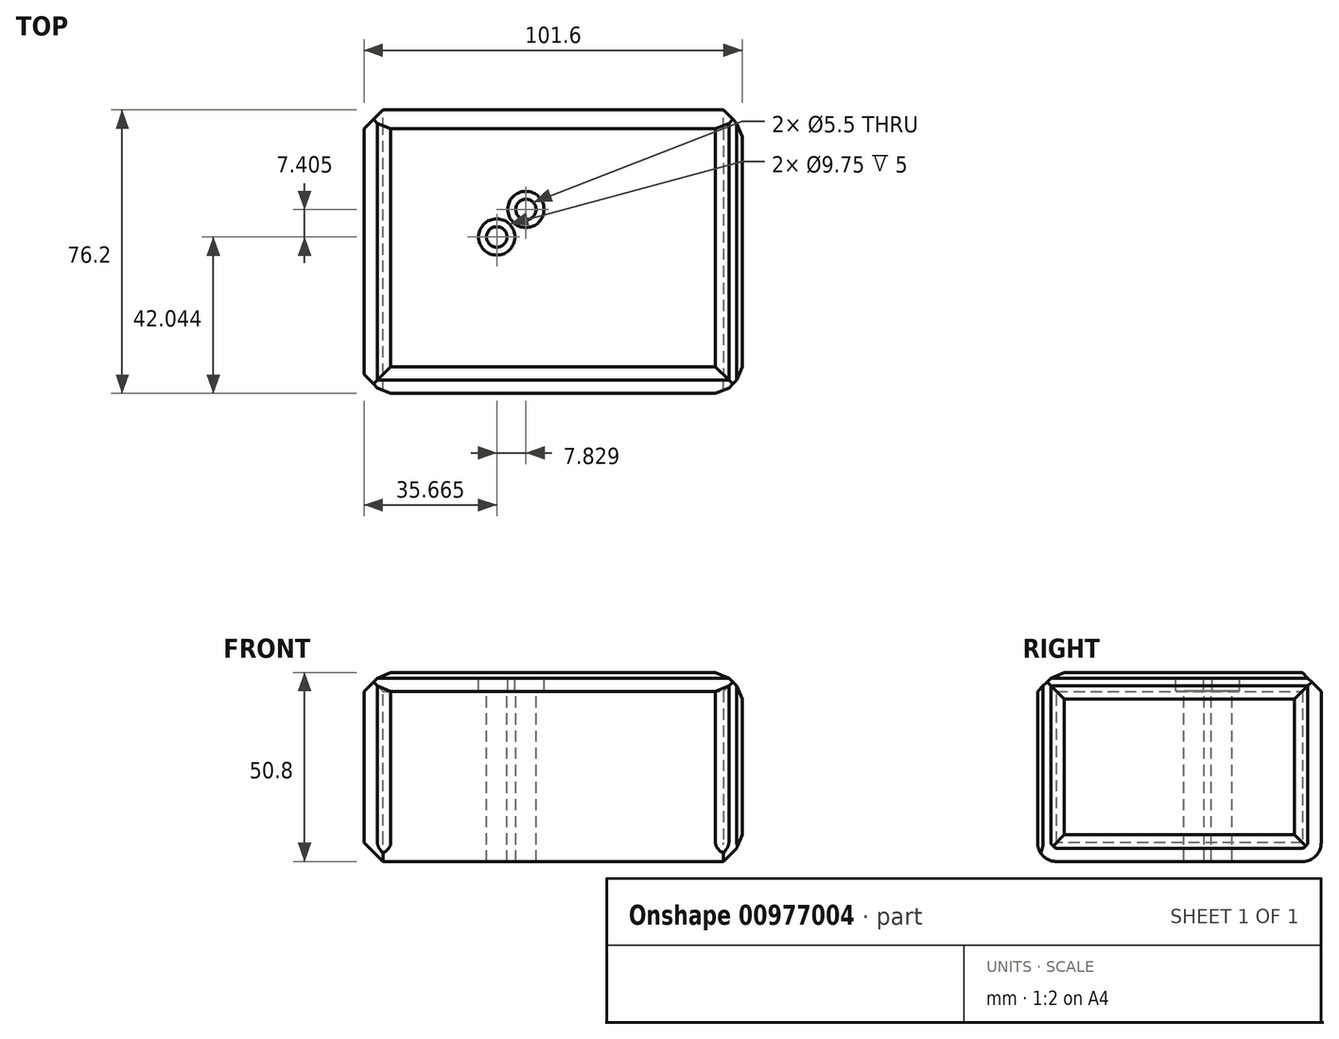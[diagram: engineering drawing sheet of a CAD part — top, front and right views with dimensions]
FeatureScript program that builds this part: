
annotation { "Feature Type Name" : "Feature", "Feature Type Description" : "" }
export const myFeature = defineFeature(function(context is Context, id is Id, definition is map)
    precondition{}
    {
        {
            var Q0;
            Q0=qCreatedBy(makeId("Top.planeOp"),FACE);
            var sketch = newSketch(context, id + "F0", { "sketchPlane" : qUnion([Q0])});
            skLineSegment(sketch, "E0.bottom", {"start": v(50.8, 38.1) * mm, "end": v(-50.8, 38.1) * mm});
            skLineSegment(sketch, "E0.top", {"start": v(50.8, -38.1) * mm, "end": v(-50.8, -38.1) * mm});
            skLineSegment(sketch, "E0.left", {"start": v(50.8, 38.1) * mm, "end": v(50.8, -38.1) * mm});
            skLineSegment(sketch, "E0.right", {"start": v(-50.8, 38.1) * mm, "end": v(-50.8, -38.1) * mm});
            skPoint(sketch, "E0.middle", {"position": v(0, 0) * mm});
            skCircle(sketch, "E1", {"center": v(0, -4.6) * mm, "radius": 3.99 * mm});
            skCircle(sketch, "E2", {"center": v(0, -4.6) * mm, "radius": 22.85 * mm});
            skSolve(sketch);
        }
        {
            var Q0;
            Q0=makeQuery(id+"F0.imprint","IMPRINT",FACE,{"disambiguationData":[TD([[makeQuery(id+"F0.imprint","IMPRINT",EDGE,{"derivedFrom":sQuery(id+"F0.wireOp",EDGE,"E0.bottom")}),1.0]])]});
            var Q1;
            Q1=makeQuery(id+"F0.imprint","IMPRINT",FACE,{"disambiguationData":[TD([[makeQuery(id+"F0.imprint","IMPRINT",EDGE,{"derivedFrom":sQuery(id+"F0.wireOp",EDGE,"E1")}),1.0]])]});
            var Q2;
            Q2=makeQuery(id+"F0.imprint","IMPRINT",FACE,{"disambiguationData":[TD([[makeQuery(id+"F0.imprint","IMPRINT",EDGE,{"derivedFrom":sQuery(id+"F0.wireOp",EDGE,"E1")}),-1.0]])]});
            extrude(context, id + "F1", {"entities" : qUnion([Q0, Q1, Q2]), "depth" : 50.8 * mm, "offsetDistance" : 25.4 * mm});
        }
        {
            var Q0;
            Q0=makeQuery(id+"F1.opExtrude","CAP_EDGE",EDGE,{"disambiguationData":[OSD([sQuery(id+"F0.wireOp",EDGE,"E0.bottom")])],"isStart":true});
            fillet(context, id + "F2", {"entities" : qUnion([Q0]), "radius" : 5.08 * mm, "tangentPropagation" : true, "allowEdgeOverflow" : false});
        }
        {
            var Q0;
            Q0=makeQuery(id+"F1.opExtrude","CAP_EDGE",EDGE,{"disambiguationData":[OSD([sQuery(id+"F0.wireOp",EDGE,"E0.top")])],"isStart":true});
            fillet(context, id + "F3", {"entities" : qUnion([Q0]), "radius" : 5.08 * mm, "tangentPropagation" : true, "allowEdgeOverflow" : false});
        }
        {
            var Q0;
            Q0=makeQuery(id+"F1.opExtrude","SWEPT_FACE",FACE,{"disambiguationData":[OSD([sQuery(id+"F0.wireOp",EDGE,"E0.left")])]});
            chamfer(context, id + "F4", {"entities" : qUnion([Q0]), "width" : 5.08 * mm, "tangentPropagation" : true});
        }
        {
            var Q0;
            Q0=makeQuery(id+"F1.opExtrude","SWEPT_FACE",FACE,{"disambiguationData":[OSD([sQuery(id+"F0.wireOp",EDGE,"E0.right")])]});
            chamfer(context, id + "F5", {"entities" : qUnion([Q0]), "width" : 5.08 * mm, "tangentPropagation" : true});
        }
        {
            var Q0;
            Q0=makeQuery(id+"F1.opExtrude","SWEPT_FACE",FACE,{"disambiguationData":[OSD([sQuery(id+"F0.wireOp",EDGE,"E0.top")])]});
            chamfer(context, id + "F6", {"entities" : qUnion([Q0]), "width" : 5.08 * mm, "tangentPropagation" : true});
        }
        {
            var Q0;
            Q0=makeQuery(id+"F1.opExtrude","CAP_FACE",FACE,{"disambiguationData":[OSD([sQuery(id+"F0.wireOp",EDGE,"E0.bottom"),sQuery(id+"F0.wireOp",EDGE,"E0.top"),sQuery(id+"F0.wireOp",EDGE,"E0.left"),sQuery(id+"F0.wireOp",EDGE,"E0.right")])],"isStart":false});
            chamfer(context, id + "F7", {"entities" : qUnion([Q0]), "width" : 5.08 * mm, "tangentPropagation" : true});
        }
        {
            var Q0;
            Q0=makeQuery(id+"F1.opExtrude","SWEPT_FACE",FACE,{"disambiguationData":[OSD([sQuery(id+"F0.wireOp",EDGE,"E0.left")])]});
            chamfer(context, id + "F8", {"entities" : qUnion([Q0]), "width" : 5.08 * mm, "tangentPropagation" : true});
        }
        {
            var Q0;
            Q0=makeQuery(id+"F1.opExtrude","CAP_FACE",FACE,{"disambiguationData":[OSD([sQuery(id+"F0.wireOp",EDGE,"E0.bottom"),sQuery(id+"F0.wireOp",EDGE,"E0.top"),sQuery(id+"F0.wireOp",EDGE,"E0.left"),sQuery(id+"F0.wireOp",EDGE,"E0.right")])],"isStart":false});
            var sketch = newSketch(context, id + "F9", { "sketchPlane" : qUnion([Q0])});
            skSolve(sketch);
        }
        {
            var Q0;
            {var subQ0=sQuery(id+"F0.wireOp",EDGE,"E0.right");var subQ1=sQuery(id+"F0.wireOp",EDGE,"E0.left");var subQ2=sQuery(id+"F0.wireOp",EDGE,"E0.top");var subQ3=sQuery(id+"F0.wireOp",EDGE,"E0.bottom");var subQ4=makeQuery(id+"F1.opExtrude","CAP_FACE",FACE,{"disambiguationData":[OSD([subQ3,subQ2,subQ1,subQ0])],"isStart":false});var subQ5=subQ4;var subQ6=subQ5;var subQ7=subQ6;Q0=makeQuery(id+"F9.imprint","IMPRINT",FACE,{"disambiguationData":[TD([[makeQuery(id+"F9.imprint","IMPRINT",EDGE,{"derivedFrom":makeQuery(id+"F7.opChamfer","BLEND_EDGE",EDGE,{"blendedFrom":[makeQuery(id+"F1.opExtrude","CAP_EDGE",EDGE,{"disambiguationData":[OSD([subQ3])],"isStart":false}),subQ7],"blendedInto":[subQ7]})}),1.0]])]});}
            var sketch = newSketch(context, id + "F10", { "sketchPlane" : qUnion([Q0])});
            skCircle(sketch, "E3", {"center": v(-7.3, 11.35) * mm, "radius": 10.78 * mm});
            skPoint(sketch, "E3.first.point", {"position": v(-12.12, 21) * mm});
            skPoint(sketch, "E3.second.point", {"position": v(0, 3.43) * mm});
            skPoint(sketch, "E3.third.point", {"position": v(-15.14, 3.94) * mm});
            skSolve(sketch);
        }
        {
            var Q0;
            Q0=sQuery(id+"F10.wireOp",VERTEX,"E3.third.point");
            var Q1;
            Q1=sQuery(id+"F10.wireOp",VERTEX,"E3.center");
            var Q2;
            Q2=makeQuery(id+"F1.opExtrude","SWEPT_BODY",BODY,{"disambiguationData":[OSD([sQuery(id+"F0.wireOp",EDGE,"E0.bottom"),sQuery(id+"F0.wireOp",EDGE,"E0.top"),sQuery(id+"F0.wireOp",EDGE,"E0.left"),sQuery(id+"F0.wireOp",EDGE,"E0.right")])]});
            hole(context, id + "F11", {"style" : HoleStyle.C_BORE, "endStyle" : HoleEndStyle.THROUGH, "standardTappedOrClearance" : lookupTablePath({ "fit" : "Normal", "standard" : "ISO", "size" : "M5", "type" : "Clearance" }), "standardBlindInLast" : lookupTablePath({ "fit" : "Normal", "standard" : "ISO", "engagement" : "75%", "pitch" : "0.8 mm", "size" : "M5", "type" : "Clearance & tapped" }), "holeDiameter" : 5.5 * mm, "cBoreDiameter" : 9.75 * mm, "cBoreDepth" : 5 * mm, "majorDiameter" : 6.35 * mm, "isTappedThrough" : true, "tappedDepth" : 12.7 * mm, "tapClearance" : 3, "startFromSketch" : true, "locations" : qUnion([Q0, Q1]), "scope" : qUnion([Q2])});
        }
    });
